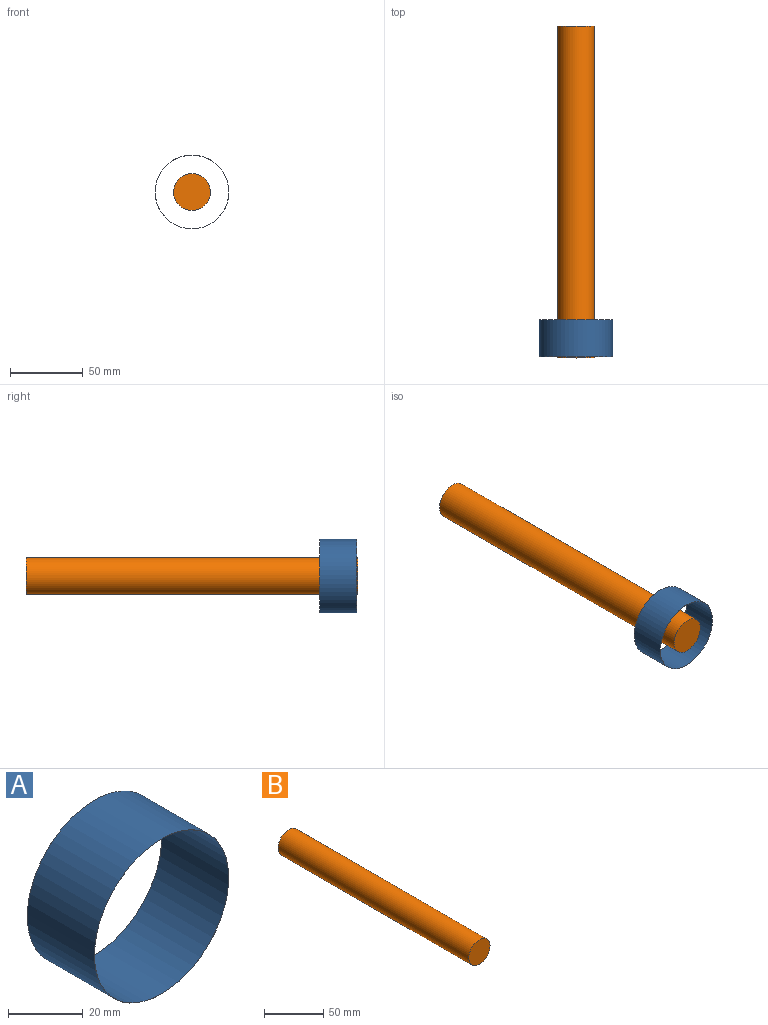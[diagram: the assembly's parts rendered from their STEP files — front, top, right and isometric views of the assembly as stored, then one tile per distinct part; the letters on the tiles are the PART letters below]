
ASSEMBLY  parts=2 mates=1
PART A: 4 faces, bbox 50.8x25.4x50.8 mm
  f0: cylinder r=25.37mm len=50.75mm, axis (0,1,0), area 4049.6mm2, adj f2,f3
  f1: cylinder r=25.4mm len=50.8mm, axis (0,1,0), area 4053.7mm2, adj f2,f3
  f2: plane 50.8x50.8mm, normal (0,-1,0), area 4.1mm2, adj f0,f1
  f3: plane 50.8x50.8mm, normal (0,1,0), area 4.1mm2, adj f0,f1
PART B: 3 faces, bbox 25.4x228.6x25.4 mm
  f0: cylinder r=12.7mm len=228.6mm, axis (0,1,0), area 18241.5mm2, adj f1,f2
  f1: plane 25.4x25.4mm, normal (0,-1,0), area 506.7mm2, adj f0
  f2: plane 25.4x25.4mm, normal (0,1,0), area 506.7mm2, adj f0
PLACE A t=(-105.54,-171.7,-18.71)mm
PLACE B t=(-105.54,30.73,-18.71)mm
MATE slider B.f0 <-> A.f0  axis (0,1,0) through (-105.54,-83.57,-18.71)mm
